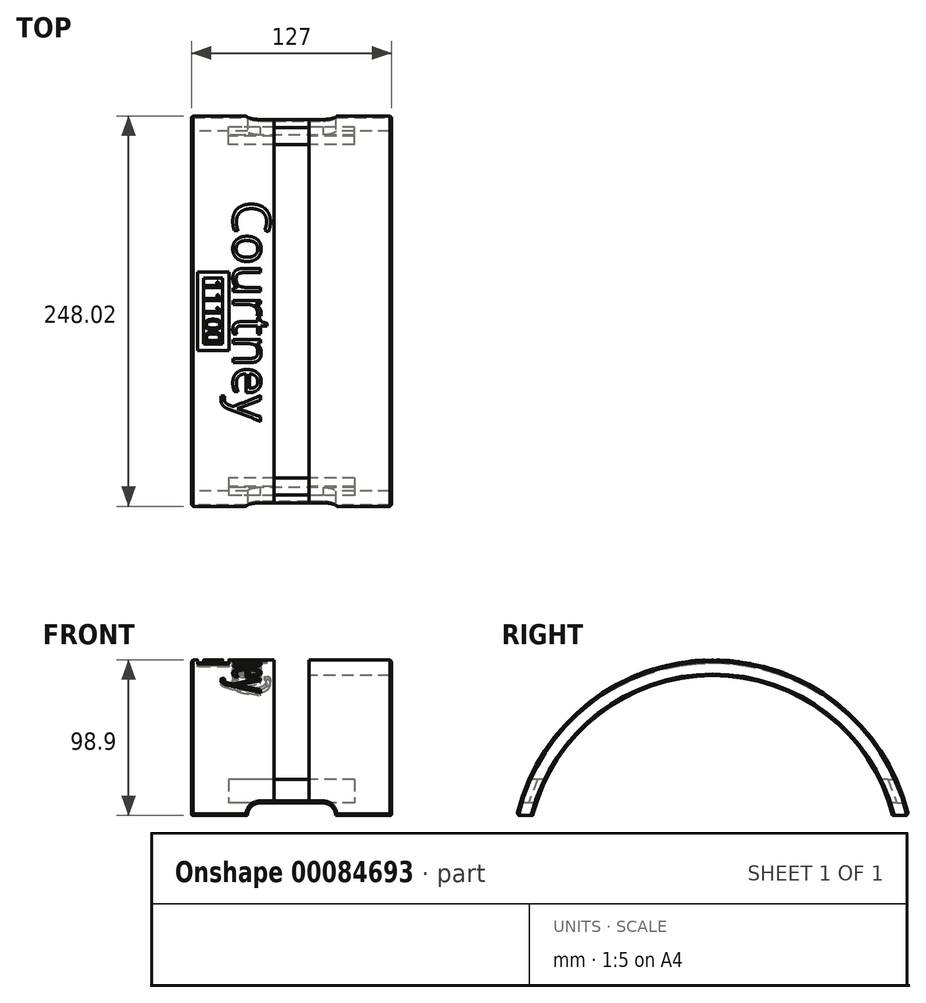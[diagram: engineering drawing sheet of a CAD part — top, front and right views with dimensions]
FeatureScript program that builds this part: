
annotation { "Feature Type Name" : "Feature", "Feature Type Description" : "" }
export const myFeature = defineFeature(function(context is Context, id is Id, definition is map)
    precondition{}
    {
        {
            var Q0;
            Q0=qCreatedBy(makeId("Right.planeOp"),FACE);
            var sketch = newSketch(context, id + "F0", { "sketchPlane" : qUnion([Q0])});
            skArc(sketch, "E0", {"start": v(114.3, 0) * mm, "mid": v(0, 88.9) * mm, "end": v(-114.3, 0) * mm});
            skPoint(sketch, "E1", {"position": v(0, 88.9) * mm});
            skArc(sketch, "E2", {"start": v(124.3, 0) * mm, "mid": v(0, 98.9) * mm, "end": v(-124.3, 0) * mm});
            skLineSegment(sketch, "E3", {"start": v(-124.3, 0) * mm, "end": v(-114.3, 0) * mm});
            skLineSegment(sketch, "E4", {"start": v(124.3, 0) * mm, "end": v(114.3, 0) * mm});
            skLineSegment(sketch, "E5", {"start": v(0, 98.9) * mm, "end": v(0, 88.9) * mm, "construction": true});
            skLineSegment(sketch, "E6", {"start": v(-114.3, 0) * mm, "end": v(114.3, 0) * mm, "construction": true});
            skLineSegment(sketch, "E7", {"start": v(10, 98.9) * mm, "end": v(-10, 98.9) * mm, "construction": true});
            skPoint(sketch, "E8", {"position": v(0, 98.9) * mm});
            skLineSegment(sketch, "E9", {"start": v(119.06, 17.12) * mm, "end": v(-119.06, 17.12) * mm});
            skPoint(sketch, "E10", {"position": v(0, 17.12) * mm});
            skPoint(sketch, "E11", {"position": v(-119.06, 17.12) * mm});
            skPoint(sketch, "E12", {"position": v(119.06, 17.12) * mm});
            skSolve(sketch);
        }
        {
            var Q0;
            Q0=makeQuery(id+"F0.imprint","IMPRINT",FACE,{"disambiguationData":[TD([[makeQuery(id+"F0.imprint","IMPRINT",EDGE,{"derivedFrom":sQuery(id+"F0.wireOp",EDGE,"E0")}),-1.0]])]});
            extrude(context, id + "F1", {"entities" : qUnion([Q0]), "depth" : 127 * mm});
        }
        {
            var Q0;
            Q0=sQuery(id+"F0.wireOp",EDGE,"E7");
            cPlane(context, id + "F2", {"entities" : qUnion([Q0]), "cplaneType" : CPlaneType.LINE_ANGLE, "offset" : 150 * mm, "angle" : 0 * degree, "width" : 150 * mm, "height" : 150 * mm});
        }
        {
            var Q0;
            Q0=makeQuery(id+"F1.opExtrude","SWEPT_EDGE",EDGE,{"disambiguationData":[OSD([sQuery(id+"F0.wireOp",EDGE,"E2"),sQuery(id+"F0.wireOp",EDGE,"E3")])]});
            cPlane(context, id + "F3", {"entities" : qUnion([Q0]), "cplaneType" : CPlaneType.LINE_ANGLE, "offset" : 150 * mm, "angle" : 0 * degree, "width" : 150 * mm, "height" : 150 * mm});
        }
        {
            var Q0;
            Q0=qCreatedBy(id+"F3.planeOp",FACE);
            var sketch = newSketch(context, id + "F4", { "sketchPlane" : qUnion([Q0])});
            skLineSegment(sketch, "E13", {"start": v(0, 98.9) * mm, "end": v(127, 98.9) * mm});
            skLineSegment(sketch, "E14.0", {"start": v(127, 98.9) * mm, "end": v(127, 0) * mm});
            skLineSegment(sketch, "E15.0", {"start": v(127, 0) * mm, "end": v(0, 0) * mm});
            skLineSegment(sketch, "E16.0", {"start": v(0, 98.9) * mm, "end": v(0, 0) * mm});
            skPoint(sketch, "E17", {"position": v(63.5, 0) * mm});
            skLineSegment(sketch, "E18", {"start": v(43.5, 8) * mm, "end": v(83.5, 8) * mm});
            skPoint(sketch, "E19", {"position": v(63.5, 8) * mm});
            skArc(sketch, "E20", {"start": v(43.5, 8) * mm, "mid": v(37.84, 5.66) * mm, "end": v(35.5, 0) * mm});
            skArc(sketch, "E21", {"start": v(91.5, 0) * mm, "mid": v(89.16, 5.66) * mm, "end": v(83.5, 8) * mm});
            skPoint(sketch, "E22.positionSnap0", {"position": v(63.5, 98.9) * mm});
            skLineSegment(sketch, "E23.bottom", {"start": v(52.5, 23) * mm, "end": v(74.5, 23) * mm});
            skLineSegment(sketch, "E23.top", {"start": v(52.5, 98.9) * mm, "end": v(74.5, 98.9) * mm});
            skLineSegment(sketch, "E23.left", {"start": v(52.5, 23) * mm, "end": v(52.5, 98.9) * mm});
            skLineSegment(sketch, "E23.right", {"start": v(74.5, 23) * mm, "end": v(74.5, 98.9) * mm});
            skSolve(sketch);
        }
        {
            var Q0;
            Q0=makeQuery(id+"F4.imprint","IMPRINT",FACE,{"disambiguationData":[TD([[makeQuery(id+"F4.imprint","IMPRINT",EDGE,{"derivedFrom":sQuery(id+"F4.wireOp",EDGE,"E23.bottom")}),1.0]])]});
            var Q1;
            Q1=makeQuery(id+"F4.imprint","IMPRINT",FACE,{"disambiguationData":[TD([[makeQuery(id+"F4.imprint","IMPRINT",EDGE,{"derivedFrom":sQuery(id+"F4.wireOp",EDGE,"E18")}),-1.0]])]});
            extrude(context, id + "F5", {"entities" : qUnion([Q0, Q1]), "operationType" : NewBodyOperationType.REMOVE, "endBound" : BoundingType.THROUGH_ALL, "oppositeDirection" : true, "depth" : 25 * mm});
        }
        {
            var Q0;
            Q0=makeQuery(id+"F5.boolean.opBoolean","COPY",FACE,{"derivedFrom":makeQuery(id+"F5.opExtrude","SWEPT_FACE",FACE,{"disambiguationData":[OSD([sQuery(id+"F4.wireOp",EDGE,"E23.left")])]})});
            var Q1;
            Q1=makeQuery(id+"F5.boolean.opBoolean","COPY",FACE,{"derivedFrom":makeQuery(id+"F5.opExtrude","SWEPT_FACE",FACE,{"disambiguationData":[OSD([sQuery(id+"F4.wireOp",EDGE,"E23.right")])]})});
            cPlane(context, id + "F6", {"entities" : qUnion([Q0, Q1]), "cplaneType" : CPlaneType.MID_PLANE, "offset" : 150 * mm, "width" : 150 * mm, "height" : 150 * mm});
        }
        {
            var Q0;
            Q0=qCreatedBy(id+"F6.planeOp",FACE);
            var sketch = newSketch(context, id + "F7", { "sketchPlane" : qUnion([Q0])});
            skArc(sketch, "E24.0", {"start": v(114.3, 0) * mm, "mid": v(0, 88.9) * mm, "end": v(-114.3, 0) * mm});
            skLineSegment(sketch, "E25.0", {"start": v(-111.96, 8) * mm, "end": v(-122.18, 8) * mm});
            skLineSegment(sketch, "E26.0", {"start": v(-105.83, 23) * mm, "end": v(-116.63, 23) * mm});
            skLineSegment(sketch, "E27", {"start": v(-111.23, 23) * mm, "end": v(-117.07, 8) * mm});
            skArc(sketch, "E28.0", {"start": v(124.3, 0) * mm, "mid": v(0, 98.9) * mm, "end": v(-124.3, 0) * mm});
            skLineSegment(sketch, "E29", {"start": v(0, 0) * mm, "end": v(0, 150) * mm, "construction": true});
            skPoint(sketch, "E29.endSnap0", {"position": v(0, 98.9) * mm});
            skLineSegment(sketch, "E30", {"start": v(75, 0) * mm, "end": v(-75, 0) * mm, "construction": true});
            skPoint(sketch, "E31", {"position": v(0, 0) * mm});
            skSolve(sketch);
        }
        {
            var Q0;
            {var subQ5=sQuery(id+"F7.wireOp",EDGE,"E27");Q0=makeQuery(id+"F7.imprint","IMPRINT",FACE,{"disambiguationData":[TD([[makeQuery(id+"F7.imprint","IMPRINT",EDGE,{"derivedFrom":subQ5}),1.0]])]});}
            extrude(context, id + "F8", {"entities" : qUnion([Q0]), "endBound" : BoundingType.SYMMETRIC, "depth" : 80 * mm});
        }
        {
            var Q0;
            {var subQ3=sQuery(id+"F7.wireOp",EDGE,"E27");Q0=makeQuery(id+"F7.imprint","IMPRINT",FACE,{"disambiguationData":[TD([[makeQuery(id+"F7.imprint","IMPRINT",EDGE,{"derivedFrom":subQ3}),-1.0]])]});}
            var Q1;
            Q1=makeQuery(id+"F5.boolean.opBoolean","COPY",FACE,{"derivedFrom":makeQuery(id+"F5.opExtrude","SWEPT_FACE",FACE,{"disambiguationData":[OSD([sQuery(id+"F4.wireOp",EDGE,"E23.right")])]})});
            extrude(context, id + "F9", {"entities" : qUnion([Q0]), "endBound" : BoundingType.UP_TO_SURFACE, "endBoundEntityFace" : qUnion([Q1]), "depth" : 25 * mm});
        }
        {
            var Q0;
            Q0=makeQuery(id+"F9.opExtrude","SWEPT_BODY",BODY,{"disambiguationData":[OSD([sQuery(id+"F7.wireOp",EDGE,"E25.0"),sQuery(id+"F7.wireOp",EDGE,"E26.0"),sQuery(id+"F7.wireOp",EDGE,"E27"),sQuery(id+"F7.wireOp",EDGE,"E28.0")])]});
            var Q1;
            {var subQ3=sQuery(id+"F7.wireOp",EDGE,"E27");Q1=makeQuery(id+"F7.imprint","IMPRINT",FACE,{"disambiguationData":[TD([[makeQuery(id+"F7.imprint","IMPRINT",EDGE,{"derivedFrom":subQ3}),-1.0]])]});}
            mirror(context, id + "F10", {"entities" : qUnion([Q0]), "mirrorPlane" : qUnion([Q1])});
        }
        {
            var Q0;
            Q0=makeQuery(id+"F10.opPattern","COPY",BODY,{"derivedFrom":makeQuery(id+"F9.opExtrude","SWEPT_BODY",BODY,{"disambiguationData":[OSD([sQuery(id+"F7.wireOp",EDGE,"E25.0"),sQuery(id+"F7.wireOp",EDGE,"E26.0"),sQuery(id+"F7.wireOp",EDGE,"E27"),sQuery(id+"F7.wireOp",EDGE,"E28.0")])]}),"instanceName":"1"});
            var Q1;
            Q1=makeQuery(id+"F9.opExtrude","SWEPT_BODY",BODY,{"disambiguationData":[OSD([sQuery(id+"F7.wireOp",EDGE,"E25.0"),sQuery(id+"F7.wireOp",EDGE,"E26.0"),sQuery(id+"F7.wireOp",EDGE,"E27"),sQuery(id+"F7.wireOp",EDGE,"E28.0")])]});
            var Q2;
            Q2=makeQuery(id+"F8.opExtrude","SWEPT_BODY",BODY,{"disambiguationData":[OSD([sQuery(id+"F7.wireOp",EDGE,"E24.0"),sQuery(id+"F7.wireOp",EDGE,"E25.0"),sQuery(id+"F7.wireOp",EDGE,"E26.0"),sQuery(id+"F7.wireOp",EDGE,"E27")])]});
            var Q3;
            Q3=makeQuery(id+"F1.opExtrude","SWEPT_BODY",BODY,{"disambiguationData":[OSD([sQuery(id+"F0.wireOp",EDGE,"E0"),sQuery(id+"F0.wireOp",EDGE,"E2"),sQuery(id+"F0.wireOp",EDGE,"E3"),sQuery(id+"F0.wireOp",EDGE,"E4")])]});
            booleanBodies(context, id + "F11", {"operationType" : BooleanOperationType.SUBTRACTION, "tools" : qUnion([Q0, Q1, Q2]), "targets" : qUnion([Q3]), "keepTools" : true});
        }
        {
            var Q0;
            Q0=makeQuery(id+"F10.opPattern","COPY",BODY,{"derivedFrom":makeQuery(id+"F9.opExtrude","SWEPT_BODY",BODY,{"disambiguationData":[OSD([sQuery(id+"F7.wireOp",EDGE,"E25.0"),sQuery(id+"F7.wireOp",EDGE,"E26.0"),sQuery(id+"F7.wireOp",EDGE,"E27"),sQuery(id+"F7.wireOp",EDGE,"E28.0")])]}),"instanceName":"1"});
            var Q1;
            Q1=makeQuery(id+"F9.opExtrude","SWEPT_BODY",BODY,{"disambiguationData":[OSD([sQuery(id+"F7.wireOp",EDGE,"E25.0"),sQuery(id+"F7.wireOp",EDGE,"E26.0"),sQuery(id+"F7.wireOp",EDGE,"E27"),sQuery(id+"F7.wireOp",EDGE,"E28.0")])]});
            var Q2;
            Q2=makeQuery(id+"F8.opExtrude","SWEPT_BODY",BODY,{"disambiguationData":[OSD([sQuery(id+"F7.wireOp",EDGE,"E24.0"),sQuery(id+"F7.wireOp",EDGE,"E25.0"),sQuery(id+"F7.wireOp",EDGE,"E26.0"),sQuery(id+"F7.wireOp",EDGE,"E27")])]});
            booleanBodies(context, id + "F12", {"operationType" : BooleanOperationType.UNION, "tools" : qUnion([Q0, Q1, Q2])});
        }
        {
            var Q0;
            Q0=makeQuery(id+"F10.opPattern","COPY",BODY,{"derivedFrom":makeQuery(id+"F9.opExtrude","SWEPT_BODY",BODY,{"disambiguationData":[OSD([sQuery(id+"F7.wireOp",EDGE,"E25.0"),sQuery(id+"F7.wireOp",EDGE,"E26.0"),sQuery(id+"F7.wireOp",EDGE,"E27"),sQuery(id+"F7.wireOp",EDGE,"E28.0")])]}),"instanceName":"1"});
            var Q1;
            Q1=qCreatedBy(makeId("Front.planeOp"),FACE);
            mirror(context, id + "F13", {"entities" : qUnion([Q0]), "mirrorPlane" : qUnion([Q1])});
        }
        {
            var Q0;
            Q0=makeQuery(id+"F13.opPattern","COPY",BODY,{"derivedFrom":makeQuery(id+"F10.opPattern","COPY",BODY,{"derivedFrom":makeQuery(id+"F9.opExtrude","SWEPT_BODY",BODY,{"disambiguationData":[OSD([sQuery(id+"F7.wireOp",EDGE,"E25.0"),sQuery(id+"F7.wireOp",EDGE,"E26.0"),sQuery(id+"F7.wireOp",EDGE,"E27"),sQuery(id+"F7.wireOp",EDGE,"E28.0")])]}),"instanceName":"1"}),"instanceName":"1"});
            var Q1;
            Q1=makeQuery(id+"F1.opExtrude","SWEPT_BODY",BODY,{"disambiguationData":[OSD([sQuery(id+"F0.wireOp",EDGE,"E0"),sQuery(id+"F0.wireOp",EDGE,"E2"),sQuery(id+"F0.wireOp",EDGE,"E3"),sQuery(id+"F0.wireOp",EDGE,"E4")])]});
            booleanBodies(context, id + "F14", {"operationType" : BooleanOperationType.SUBTRACTION, "tools" : qUnion([Q0]), "targets" : qUnion([Q1]), "keepTools" : true});
        }
        {
            var Q0;
            Q0=makeQuery(id+"F1.opExtrude","CAP_EDGE",EDGE,{"disambiguationData":[OSD([sQuery(id+"F0.wireOp",EDGE,"E2")])],"isStart":true});
            var Q1;
            Q1=makeQuery(id+"F1.opExtrude","CAP_EDGE",EDGE,{"disambiguationData":[OSD([sQuery(id+"F0.wireOp",EDGE,"E0")])],"isStart":true});
            var Q2;
            Q2=makeQuery(id+"F5.boolean.opBoolean","INTERSECT",EDGE,{"disambiguationData":[OD(1.0)],"derivedFrom":[makeQuery(id+"F1.opExtrude","SWEPT_FACE",FACE,{"disambiguationData":[OSD([sQuery(id+"F0.wireOp",EDGE,"E2")])]}),makeQuery(id+"F5.opExtrude","SWEPT_FACE",FACE,{"disambiguationData":[OSD([sQuery(id+"F4.wireOp",EDGE,"E21")])]})]});
            var Q3;
            {var subQ0=makeQuery(id+"F5.opExtrude","SWEPT_FACE",FACE,{"disambiguationData":[OSD([sQuery(id+"F4.wireOp",EDGE,"E18")])]});var subQ2=makeQuery(id+"F1.opExtrude","SWEPT_FACE",FACE,{"disambiguationData":[OSD([sQuery(id+"F0.wireOp",EDGE,"E2")])]});Q3=makeQuery(id+"F14.opBoolean","SPLIT",EDGE,{"disambiguationData":[TD([makeQuery(id+"F5.boolean.opBoolean","COPY",FACE,{"derivedFrom":makeQuery(id+"F5.opExtrude","SWEPT_FACE",FACE,{"disambiguationData":[OSD([sQuery(id+"F4.wireOp",EDGE,"E23.right")])]})})])],"derivedFrom":makeQuery(id+"F5.boolean.opBoolean","INTERSECT",EDGE,{"disambiguationData":[OD(1.0)],"derivedFrom":[subQ2,subQ0]})});}
            var Q4;
            {var subQ0=makeQuery(id+"F9.opExtrude","SWEPT_EDGE",EDGE,{"disambiguationData":[OSD([sQuery(id+"F7.wireOp",EDGE,"E25.0"),sQuery(id+"F7.wireOp",EDGE,"E28.0")])]});Q4=makeQuery(id+"F13.opPattern","COPY",EDGE,{"derivedFrom":makeQuery(id+"F12.opBoolean","MERGE",EDGE,{"derivedFrom":[subQ0,makeQuery(id+"F10.opPattern","COPY",EDGE,{"derivedFrom":subQ0,"instanceName":"1"})]}),"instanceName":"1"});}
            var Q5;
            Q5=makeQuery(id+"F5.boolean.opBoolean","INTERSECT",EDGE,{"disambiguationData":[OD(1.0)],"derivedFrom":[makeQuery(id+"F1.opExtrude","SWEPT_FACE",FACE,{"disambiguationData":[OSD([sQuery(id+"F0.wireOp",EDGE,"E2")])]}),makeQuery(id+"F5.opExtrude","SWEPT_FACE",FACE,{"disambiguationData":[OSD([sQuery(id+"F4.wireOp",EDGE,"E20")])]})]});
            var Q6;
            {var subQ0=makeQuery(id+"F5.opExtrude","SWEPT_FACE",FACE,{"disambiguationData":[OSD([sQuery(id+"F4.wireOp",EDGE,"E18")])]});var subQ1=makeQuery(id+"F1.opExtrude","SWEPT_FACE",FACE,{"disambiguationData":[OSD([sQuery(id+"F0.wireOp",EDGE,"E2")])]});Q6=makeQuery(id+"F14.opBoolean","SPLIT",EDGE,{"disambiguationData":[TD([makeQuery(id+"F5.boolean.opBoolean","COPY",FACE,{"derivedFrom":makeQuery(id+"F5.opExtrude","SWEPT_FACE",FACE,{"disambiguationData":[OSD([sQuery(id+"F4.wireOp",EDGE,"E23.left")])]})})])],"derivedFrom":makeQuery(id+"F5.boolean.opBoolean","INTERSECT",EDGE,{"disambiguationData":[OD(1.0)],"derivedFrom":[subQ1,subQ0]})});}
            var Q7;
            {var subQ0=sQuery(id+"F0.wireOp",EDGE,"E4");var subQ1=sQuery(id+"F0.wireOp",EDGE,"E2");Q7=makeQuery(id+"F5.boolean.opBoolean","SPLIT",EDGE,{"disambiguationData":[TD([makeQuery(id+"F5.opExtrude","SWEPT_FACE",FACE,{"disambiguationData":[OSD([sQuery(id+"F4.wireOp",EDGE,"E21")])]})])],"derivedFrom":makeQuery(id+"F1.opExtrude","SWEPT_EDGE",EDGE,{"disambiguationData":[OSD([subQ1,subQ0])]})});}
            var Q8;
            Q8=makeQuery(id+"F1.opExtrude","CAP_EDGE",EDGE,{"disambiguationData":[OSD([sQuery(id+"F0.wireOp",EDGE,"E2")])],"isStart":false});
            var Q9;
            Q9=makeQuery(id+"F1.opExtrude","CAP_EDGE",EDGE,{"disambiguationData":[OSD([sQuery(id+"F0.wireOp",EDGE,"E0")])],"isStart":false});
            var Q10;
            {var subQ0=sQuery(id+"F0.wireOp",EDGE,"E4");var subQ1=sQuery(id+"F0.wireOp",EDGE,"E2");Q10=makeQuery(id+"F5.boolean.opBoolean","SPLIT",EDGE,{"disambiguationData":[TD([makeQuery(id+"F5.opExtrude","SWEPT_FACE",FACE,{"disambiguationData":[OSD([sQuery(id+"F4.wireOp",EDGE,"E20")])]})])],"derivedFrom":makeQuery(id+"F1.opExtrude","SWEPT_EDGE",EDGE,{"disambiguationData":[OSD([subQ1,subQ0])]})});}
            var Q11;
            Q11=makeQuery(id+"F5.boolean.opBoolean","INTERSECT",EDGE,{"disambiguationData":[OD(0.0)],"derivedFrom":[makeQuery(id+"F1.opExtrude","SWEPT_FACE",FACE,{"disambiguationData":[OSD([sQuery(id+"F0.wireOp",EDGE,"E2")])]}),makeQuery(id+"F5.opExtrude","SWEPT_FACE",FACE,{"disambiguationData":[OSD([sQuery(id+"F4.wireOp",EDGE,"E20")])]})]});
            var Q12;
            {var subQ0=makeQuery(id+"F5.opExtrude","SWEPT_FACE",FACE,{"disambiguationData":[OSD([sQuery(id+"F4.wireOp",EDGE,"E18")])]});var subQ1=makeQuery(id+"F1.opExtrude","SWEPT_FACE",FACE,{"disambiguationData":[OSD([sQuery(id+"F0.wireOp",EDGE,"E2")])]});Q12=makeQuery(id+"F11.opBoolean","SPLIT",EDGE,{"disambiguationData":[TD([makeQuery(id+"F5.boolean.opBoolean","COPY",FACE,{"derivedFrom":makeQuery(id+"F5.opExtrude","SWEPT_FACE",FACE,{"disambiguationData":[OSD([sQuery(id+"F4.wireOp",EDGE,"E23.left")])]})})])],"derivedFrom":makeQuery(id+"F5.boolean.opBoolean","INTERSECT",EDGE,{"disambiguationData":[OD(0.0)],"derivedFrom":[subQ1,subQ0]})});}
            var Q13;
            {var subQ0=makeQuery(id+"F9.opExtrude","SWEPT_EDGE",EDGE,{"disambiguationData":[OSD([sQuery(id+"F7.wireOp",EDGE,"E25.0"),sQuery(id+"F7.wireOp",EDGE,"E28.0")])]});Q13=makeQuery(id+"F12.opBoolean","MERGE",EDGE,{"derivedFrom":[subQ0,makeQuery(id+"F10.opPattern","COPY",EDGE,{"derivedFrom":subQ0,"instanceName":"1"})]});}
            var Q14;
            {var subQ0=makeQuery(id+"F5.opExtrude","SWEPT_FACE",FACE,{"disambiguationData":[OSD([sQuery(id+"F4.wireOp",EDGE,"E18")])]});var subQ1=makeQuery(id+"F1.opExtrude","SWEPT_FACE",FACE,{"disambiguationData":[OSD([sQuery(id+"F0.wireOp",EDGE,"E2")])]});Q14=makeQuery(id+"F11.opBoolean","SPLIT",EDGE,{"disambiguationData":[TD([makeQuery(id+"F5.boolean.opBoolean","COPY",FACE,{"derivedFrom":makeQuery(id+"F5.opExtrude","SWEPT_FACE",FACE,{"disambiguationData":[OSD([sQuery(id+"F4.wireOp",EDGE,"E23.right")])]})})])],"derivedFrom":makeQuery(id+"F5.boolean.opBoolean","INTERSECT",EDGE,{"disambiguationData":[OD(0.0)],"derivedFrom":[subQ1,subQ0]})});}
            var Q15;
            Q15=makeQuery(id+"F5.boolean.opBoolean","INTERSECT",EDGE,{"disambiguationData":[OD(0.0)],"derivedFrom":[makeQuery(id+"F1.opExtrude","SWEPT_FACE",FACE,{"disambiguationData":[OSD([sQuery(id+"F0.wireOp",EDGE,"E2")])]}),makeQuery(id+"F5.opExtrude","SWEPT_FACE",FACE,{"disambiguationData":[OSD([sQuery(id+"F4.wireOp",EDGE,"E21")])]})]});
            var Q16;
            {var subQ0=sQuery(id+"F0.wireOp",EDGE,"E3");var subQ1=sQuery(id+"F0.wireOp",EDGE,"E2");Q16=makeQuery(id+"F5.boolean.opBoolean","SPLIT",EDGE,{"disambiguationData":[TD([makeQuery(id+"F5.opExtrude","SWEPT_FACE",FACE,{"disambiguationData":[OSD([sQuery(id+"F4.wireOp",EDGE,"E21")])]})])],"derivedFrom":makeQuery(id+"F1.opExtrude","SWEPT_EDGE",EDGE,{"disambiguationData":[OSD([subQ1,subQ0])]})});}
            var Q17;
            {var subQ0=sQuery(id+"F0.wireOp",EDGE,"E3");var subQ1=sQuery(id+"F0.wireOp",EDGE,"E2");Q17=makeQuery(id+"F5.boolean.opBoolean","SPLIT",EDGE,{"disambiguationData":[TD([makeQuery(id+"F5.opExtrude","SWEPT_FACE",FACE,{"disambiguationData":[OSD([sQuery(id+"F4.wireOp",EDGE,"E20")])]})])],"derivedFrom":makeQuery(id+"F1.opExtrude","SWEPT_EDGE",EDGE,{"disambiguationData":[OSD([subQ1,subQ0])]})});}
            chamfer(context, id + "F15", {"entities" : qUnion([Q0, Q1, Q2, Q3, Q4, Q5, Q6, Q7, Q8, Q9, Q10, Q11, Q12, Q13, Q14, Q15, Q16, Q17]), "width" : 1 * mm});
        }
        {
            var Q0;
            {var subQ0=sQuery(id+"F0.wireOp",EDGE,"E3");var subQ1=sQuery(id+"F0.wireOp",EDGE,"E2");var subQ2=makeQuery(id+"F5.opExtrude","SWEPT_FACE",FACE,{"disambiguationData":[OSD([sQuery(id+"F4.wireOp",EDGE,"E20")])]});var subQ3=makeQuery(id+"F1.opExtrude","SWEPT_FACE",FACE,{"disambiguationData":[OSD([subQ1])]});Q0=makeQuery(id+"F15.opChamfer","BLEND_EDGE",EDGE,{"blendedFrom":[makeQuery(id+"F5.boolean.opBoolean","INTERSECT",EDGE,{"disambiguationData":[OD(0.0)],"derivedFrom":[subQ3,subQ2]}),makeQuery(id+"F5.boolean.opBoolean","SPLIT",EDGE,{"disambiguationData":[TD([subQ2])],"derivedFrom":makeQuery(id+"F1.opExtrude","SWEPT_EDGE",EDGE,{"disambiguationData":[OSD([subQ1,subQ0])]})})],"blendedInto":[]});}
            var Q1;
            {var subQ0=sQuery(id+"F0.wireOp",EDGE,"E3");var subQ1=sQuery(id+"F0.wireOp",EDGE,"E2");Q1=makeQuery(id+"F15.opChamfer","BLEND_EDGE",EDGE,{"blendedFrom":[makeQuery(id+"F1.opExtrude","CAP_EDGE",EDGE,{"disambiguationData":[OSD([subQ1])],"isStart":true}),makeQuery(id+"F5.boolean.opBoolean","SPLIT",EDGE,{"disambiguationData":[TD([makeQuery(id+"F5.opExtrude","SWEPT_FACE",FACE,{"disambiguationData":[OSD([sQuery(id+"F4.wireOp",EDGE,"E20")])]})])],"derivedFrom":makeQuery(id+"F1.opExtrude","SWEPT_EDGE",EDGE,{"disambiguationData":[OSD([subQ1,subQ0])]})})],"blendedInto":[]});}
            var Q2;
            {var subQ0=sQuery(id+"F0.wireOp",EDGE,"E3");var subQ1=sQuery(id+"F0.wireOp",EDGE,"E2");var subQ2=makeQuery(id+"F1.opExtrude","SWEPT_FACE",FACE,{"disambiguationData":[OSD([subQ1])]});var subQ3=makeQuery(id+"F5.opExtrude","SWEPT_FACE",FACE,{"disambiguationData":[OSD([sQuery(id+"F4.wireOp",EDGE,"E21")])]});Q2=makeQuery(id+"F15.opChamfer","BLEND_EDGE",EDGE,{"blendedFrom":[makeQuery(id+"F5.boolean.opBoolean","INTERSECT",EDGE,{"disambiguationData":[OD(0.0)],"derivedFrom":[subQ2,subQ3]}),makeQuery(id+"F5.boolean.opBoolean","SPLIT",EDGE,{"disambiguationData":[TD([subQ3])],"derivedFrom":makeQuery(id+"F1.opExtrude","SWEPT_EDGE",EDGE,{"disambiguationData":[OSD([subQ1,subQ0])]})})],"blendedInto":[]});}
            var Q3;
            {var subQ0=sQuery(id+"F0.wireOp",EDGE,"E3");var subQ1=sQuery(id+"F0.wireOp",EDGE,"E2");Q3=makeQuery(id+"F15.opChamfer","BLEND_EDGE",EDGE,{"blendedFrom":[makeQuery(id+"F1.opExtrude","CAP_EDGE",EDGE,{"disambiguationData":[OSD([subQ1])],"isStart":false}),makeQuery(id+"F5.boolean.opBoolean","SPLIT",EDGE,{"disambiguationData":[TD([makeQuery(id+"F5.opExtrude","SWEPT_FACE",FACE,{"disambiguationData":[OSD([sQuery(id+"F4.wireOp",EDGE,"E21")])]})])],"derivedFrom":makeQuery(id+"F1.opExtrude","SWEPT_EDGE",EDGE,{"disambiguationData":[OSD([subQ1,subQ0])]})})],"blendedInto":[]});}
            var Q4;
            {var subQ0=sQuery(id+"F0.wireOp",EDGE,"E4");var subQ1=sQuery(id+"F0.wireOp",EDGE,"E2");Q4=makeQuery(id+"F15.opChamfer","BLEND_EDGE",EDGE,{"blendedFrom":[makeQuery(id+"F1.opExtrude","CAP_EDGE",EDGE,{"disambiguationData":[OSD([subQ1])],"isStart":false}),makeQuery(id+"F5.boolean.opBoolean","SPLIT",EDGE,{"disambiguationData":[TD([makeQuery(id+"F5.opExtrude","SWEPT_FACE",FACE,{"disambiguationData":[OSD([sQuery(id+"F4.wireOp",EDGE,"E21")])]})])],"derivedFrom":makeQuery(id+"F1.opExtrude","SWEPT_EDGE",EDGE,{"disambiguationData":[OSD([subQ1,subQ0])]})})],"blendedInto":[]});}
            var Q5;
            {var subQ0=makeQuery(id+"F5.opExtrude","SWEPT_FACE",FACE,{"disambiguationData":[OSD([sQuery(id+"F4.wireOp",EDGE,"E21")])]});var subQ1=sQuery(id+"F0.wireOp",EDGE,"E2");var subQ2=makeQuery(id+"F1.opExtrude","SWEPT_FACE",FACE,{"disambiguationData":[OSD([subQ1])]});var subQ3=sQuery(id+"F0.wireOp",EDGE,"E4");Q5=makeQuery(id+"F15.opChamfer","BLEND_EDGE",EDGE,{"blendedFrom":[makeQuery(id+"F5.boolean.opBoolean","SPLIT",EDGE,{"disambiguationData":[TD([subQ0])],"derivedFrom":makeQuery(id+"F1.opExtrude","SWEPT_EDGE",EDGE,{"disambiguationData":[OSD([subQ1,subQ3])]})}),makeQuery(id+"F5.boolean.opBoolean","INTERSECT",EDGE,{"disambiguationData":[OD(1.0)],"derivedFrom":[subQ2,subQ0]})],"blendedInto":[]});}
            var Q6;
            {var subQ0=makeQuery(id+"F5.opExtrude","SWEPT_FACE",FACE,{"disambiguationData":[OSD([sQuery(id+"F4.wireOp",EDGE,"E20")])]});var subQ1=sQuery(id+"F0.wireOp",EDGE,"E2");var subQ2=makeQuery(id+"F1.opExtrude","SWEPT_FACE",FACE,{"disambiguationData":[OSD([subQ1])]});var subQ3=sQuery(id+"F0.wireOp",EDGE,"E4");Q6=makeQuery(id+"F15.opChamfer","BLEND_EDGE",EDGE,{"blendedFrom":[makeQuery(id+"F5.boolean.opBoolean","SPLIT",EDGE,{"disambiguationData":[TD([subQ0])],"derivedFrom":makeQuery(id+"F1.opExtrude","SWEPT_EDGE",EDGE,{"disambiguationData":[OSD([subQ1,subQ3])]})}),makeQuery(id+"F5.boolean.opBoolean","INTERSECT",EDGE,{"disambiguationData":[OD(1.0)],"derivedFrom":[subQ2,subQ0]})],"blendedInto":[]});}
            var Q7;
            {var subQ0=sQuery(id+"F0.wireOp",EDGE,"E4");var subQ1=sQuery(id+"F0.wireOp",EDGE,"E2");Q7=makeQuery(id+"F15.opChamfer","BLEND_EDGE",EDGE,{"blendedFrom":[makeQuery(id+"F1.opExtrude","CAP_EDGE",EDGE,{"disambiguationData":[OSD([subQ1])],"isStart":true}),makeQuery(id+"F5.boolean.opBoolean","SPLIT",EDGE,{"disambiguationData":[TD([makeQuery(id+"F5.opExtrude","SWEPT_FACE",FACE,{"disambiguationData":[OSD([sQuery(id+"F4.wireOp",EDGE,"E20")])]})])],"derivedFrom":makeQuery(id+"F1.opExtrude","SWEPT_EDGE",EDGE,{"disambiguationData":[OSD([subQ1,subQ0])]})})],"blendedInto":[]});}
            var Q8;
            Q8=makeQuery(id+"F1.opExtrude","CAP_EDGE",EDGE,{"disambiguationData":[OSD([sQuery(id+"F0.wireOp",EDGE,"E4")])],"isStart":true});
            var Q9;
            Q9=makeQuery(id+"F1.opExtrude","CAP_EDGE",EDGE,{"disambiguationData":[OSD([sQuery(id+"F0.wireOp",EDGE,"E4")])],"isStart":false});
            var Q10;
            Q10=makeQuery(id+"F1.opExtrude","CAP_EDGE",EDGE,{"disambiguationData":[OSD([sQuery(id+"F0.wireOp",EDGE,"E3")])],"isStart":true});
            var Q11;
            Q11=makeQuery(id+"F1.opExtrude","CAP_EDGE",EDGE,{"disambiguationData":[OSD([sQuery(id+"F0.wireOp",EDGE,"E3")])],"isStart":false});
            fillet(context, id + "F16", {"entities" : qUnion([Q0, Q1, Q2, Q3, Q4, Q5, Q6, Q7, Q8, Q9, Q10, Q11]), "radius" : 1 * mm, "tangentPropagation" : true, "allowEdgeOverflow" : false});
        }
        {
            var Q0;
            Q0=qCreatedBy(makeId("Top.planeOp"),FACE);
            cPlane(context, id + "F17", {"entities" : qUnion([Q0]), "cplaneType" : CPlaneType.OFFSET, "offset" : 102 * mm, "width" : 150 * mm, "height" : 150 * mm});
        }
        {
            var Q0;
            Q0=qCreatedBy(id+"F17.planeOp",FACE);
            var sketch = newSketch(context, id + "F18", { "sketchPlane" : qUnion([Q0])});
            skText(sketch, "E32", { "text": "Courtney", "fontName": "OpenSans-Regular.ttf"});
            skLineSegment(sketch, "E33.0", {"start": v(52.5, 121.78) * mm, "end": v(52.5, -121.78) * mm});
            skLineSegment(sketch, "E34.0", {"start": v(33.87, 124) * mm, "end": v(1.8, 124) * mm});
            skLineSegment(sketch, "E35.0", {"start": v(1, 123.84) * mm, "end": v(1, -123.84) * mm});
            skLineSegment(sketch, "E36.0", {"start": v(1.8, -124) * mm, "end": v(33.87, -124) * mm});
            skLineSegment(sketch, "E37.top", {"start": v(52.5, -121.78) * mm, "end": v(1, -121.78) * mm});
            skText(sketch, "E38", { "text": "11100", "fontName": "OpenSans-Regular.ttf"});
            skLineSegment(sketch, "E39", {"start": v(26.5, 0) * mm, "end": v(18.87, 0) * mm, "construction": true});
            skLineSegment(sketch, "E40", {"start": v(8.62, 0) * mm, "end": v(1, 0) * mm, "construction": true});
            skLineSegment(sketch, "E41.bottom", {"start": v(19.75, -21) * mm, "end": v(7.75, -21) * mm});
            skLineSegment(sketch, "E41.top", {"start": v(19.75, 21) * mm, "end": v(7.75, 21) * mm});
            skLineSegment(sketch, "E41.left", {"start": v(19.75, -21) * mm, "end": v(19.75, 21) * mm});
            skLineSegment(sketch, "E41.right", {"start": v(7.75, -21) * mm, "end": v(7.75, 21) * mm});
            skPoint(sketch, "E41.middle", {"position": v(13.75, 0) * mm});
            skLineSegment(sketch, "E42.bottom", {"start": v(23.75, -25) * mm, "end": v(3.75, -25) * mm});
            skLineSegment(sketch, "E42.top", {"start": v(23.75, 25) * mm, "end": v(3.75, 25) * mm});
            skLineSegment(sketch, "E42.left", {"start": v(23.75, -25) * mm, "end": v(23.75, 25) * mm});
            skLineSegment(sketch, "E42.right", {"start": v(3.75, -25) * mm, "end": v(3.75, 25) * mm});
            skLineSegment(sketch, "E43", {"start": v(13.75, -25) * mm, "end": v(13.75, -21) * mm, "construction": true});
            skLineSegment(sketch, "E44", {"start": v(23.75, 0) * mm, "end": v(19.75, 0) * mm, "construction": true});
            skLineSegment(sketch, "E45", {"start": v(23.75, -0.91) * mm, "end": v(19.75, -0.91) * mm, "construction": true});
            const initialGuessF18  = {"E32": [0.0265, 0.07, 0, -1, 0.0235], "E38": [0.00862, 0.02, 0, -1, 0.01025]};
            skSetInitialGuess(sketch, initialGuessF18);
            skSolve(sketch);
        }
        {
            var Q0;
            Q0=makeQuery(id+"F18.imprint","IMPRINT",FACE,{"disambiguationData":[TD([[makeQuery(id+"F18.imprint","IMPRINT",EDGE,{"derivedFrom":sQuery(id+"F18.wireOp",EDGE,"E38.sketch_text.stroke-27")}),-1.0]])]});
            var Q1;
            Q1=makeQuery(id+"F18.imprint","IMPRINT",FACE,{"disambiguationData":[TD([[makeQuery(id+"F18.imprint","IMPRINT",EDGE,{"derivedFrom":sQuery(id+"F18.wireOp",EDGE,"E38.sketch_text.stroke-43")}),-1.0]])]});
            var Q2;
            Q2=makeQuery(id+"F18.imprint","IMPRINT",FACE,{"disambiguationData":[TD([[makeQuery(id+"F18.imprint","IMPRINT",EDGE,{"derivedFrom":sQuery(id+"F18.wireOp",EDGE,"E38.sketch_text.stroke-18")}),-1.0]])]});
            var Q3;
            Q3=makeQuery(id+"F18.imprint","IMPRINT",FACE,{"disambiguationData":[TD([[makeQuery(id+"F18.imprint","IMPRINT",EDGE,{"derivedFrom":sQuery(id+"F18.wireOp",EDGE,"E38.sketch_text.stroke-9")}),-1.0]])]});
            var Q4;
            Q4=makeQuery(id+"F18.imprint","IMPRINT",FACE,{"disambiguationData":[TD([[makeQuery(id+"F18.imprint","IMPRINT",EDGE,{"derivedFrom":sQuery(id+"F18.wireOp",EDGE,"E38.sketch_text.stroke-0")}),-1.0]])]});
            var Q5;
            Q5=makeQuery(id+"F18.imprint","IMPRINT",FACE,{"disambiguationData":[TD([[makeQuery(id+"F18.imprint","IMPRINT",EDGE,{"derivedFrom":sQuery(id+"F18.wireOp",EDGE,"E41.bottom")}),1.0]])]});
            var Q6;
            Q6=makeQuery(id+"F18.imprint","IMPRINT",FACE,{"disambiguationData":[TD([[makeQuery(id+"F18.imprint","IMPRINT",EDGE,{"derivedFrom":sQuery(id+"F18.wireOp",EDGE,"E32.sketch_text.stroke-15")}),-1.0]])]});
            var Q7;
            Q7=makeQuery(id+"F18.imprint","IMPRINT",FACE,{"disambiguationData":[TD([[makeQuery(id+"F18.imprint","IMPRINT",EDGE,{"derivedFrom":sQuery(id+"F18.wireOp",EDGE,"E32.sketch_text.stroke-0")}),-1.0]])]});
            var Q8;
            Q8=makeQuery(id+"F18.imprint","IMPRINT",FACE,{"disambiguationData":[TD([[makeQuery(id+"F18.imprint","IMPRINT",EDGE,{"derivedFrom":sQuery(id+"F18.wireOp",EDGE,"E32.sketch_text.stroke-32")}),-1.0]])]});
            var Q9;
            Q9=makeQuery(id+"F18.imprint","IMPRINT",FACE,{"disambiguationData":[TD([[makeQuery(id+"F18.imprint","IMPRINT",EDGE,{"derivedFrom":sQuery(id+"F18.wireOp",EDGE,"E32.sketch_text.stroke-49")}),-1.0]])]});
            var Q10;
            Q10=makeQuery(id+"F18.imprint","IMPRINT",FACE,{"disambiguationData":[TD([[makeQuery(id+"F18.imprint","IMPRINT",EDGE,{"derivedFrom":sQuery(id+"F18.wireOp",EDGE,"E32.sketch_text.stroke-62")}),-1.0]])]});
            var Q11;
            Q11=makeQuery(id+"F18.imprint","IMPRINT",FACE,{"disambiguationData":[TD([[makeQuery(id+"F18.imprint","IMPRINT",EDGE,{"derivedFrom":sQuery(id+"F18.wireOp",EDGE,"E32.sketch_text.stroke-81")}),-1.0]])]});
            var Q12;
            Q12=makeQuery(id+"F18.imprint","IMPRINT",FACE,{"disambiguationData":[TD([[makeQuery(id+"F18.imprint","IMPRINT",EDGE,{"derivedFrom":sQuery(id+"F18.wireOp",EDGE,"E32.sketch_text.stroke-98")}),-1.0]])]});
            var Q13;
            Q13=makeQuery(id+"F18.imprint","IMPRINT",FACE,{"disambiguationData":[TD([[makeQuery(id+"F18.imprint","IMPRINT",EDGE,{"derivedFrom":sQuery(id+"F18.wireOp",EDGE,"E32.sketch_text.stroke-117")}),-1.0]])]});
            var Q14;
            {var subQ4=sQuery(id+"F0.wireOp",EDGE,"E2");Q14=makeQuery(id+"F14.opBoolean","SPLIT",FACE,{"disambiguationData":[TD([makeQuery(id+"F5.boolean.opBoolean","COPY",FACE,{"derivedFrom":makeQuery(id+"F5.opExtrude","SWEPT_FACE",FACE,{"disambiguationData":[OSD([sQuery(id+"F4.wireOp",EDGE,"E23.left")])]})})])],"derivedFrom":makeQuery(id+"F1.opExtrude","SWEPT_FACE",FACE,{"disambiguationData":[OSD([subQ4])]})});}
            extrude(context, id + "F19", {"entities" : qUnion([Q0, Q1, Q2, Q3, Q4, Q5, Q6, Q7, Q8, Q9, Q10, Q11, Q12, Q13]), "endBound" : BoundingType.UP_TO_SURFACE, "oppositeDirection" : true, "endBoundEntityFace" : qUnion([Q14]), "depth" : 25 * mm});
        }
        {
            var Q0;
            Q0=makeQuery(id+"F19.opExtrude","SWEPT_BODY",BODY,{"disambiguationData":[OSD([sQuery(id+"F18.wireOp",EDGE,"E32.sketch_text.stroke-0"),sQuery(id+"F18.wireOp",EDGE,"E32.sketch_text.stroke-1"),sQuery(id+"F18.wireOp",EDGE,"E32.sketch_text.stroke-2"),sQuery(id+"F18.wireOp",EDGE,"E32.sketch_text.stroke-3"),sQuery(id+"F18.wireOp",EDGE,"E32.sketch_text.stroke-4"),sQuery(id+"F18.wireOp",EDGE,"E32.sketch_text.stroke-5"),sQuery(id+"F18.wireOp",EDGE,"E32.sketch_text.stroke-6"),sQuery(id+"F18.wireOp",EDGE,"E32.sketch_text.stroke-7"),sQuery(id+"F18.wireOp",EDGE,"E32.sketch_text.stroke-8"),sQuery(id+"F18.wireOp",EDGE,"E32.sketch_text.stroke-9"),sQuery(id+"F18.wireOp",EDGE,"E32.sketch_text.stroke-10"),sQuery(id+"F18.wireOp",EDGE,"E32.sketch_text.stroke-11"),sQuery(id+"F18.wireOp",EDGE,"E32.sketch_text.stroke-12"),sQuery(id+"F18.wireOp",EDGE,"E32.sketch_text.stroke-13"),sQuery(id+"F18.wireOp",EDGE,"E32.sketch_text.stroke-14")])]});
            var Q1;
            Q1=makeQuery(id+"F19.opExtrude","SWEPT_BODY",BODY,{"disambiguationData":[OSD([sQuery(id+"F18.wireOp",EDGE,"E32.sketch_text.stroke-15"),sQuery(id+"F18.wireOp",EDGE,"E32.sketch_text.stroke-16"),sQuery(id+"F18.wireOp",EDGE,"E32.sketch_text.stroke-17"),sQuery(id+"F18.wireOp",EDGE,"E32.sketch_text.stroke-18"),sQuery(id+"F18.wireOp",EDGE,"E32.sketch_text.stroke-19"),sQuery(id+"F18.wireOp",EDGE,"E32.sketch_text.stroke-20"),sQuery(id+"F18.wireOp",EDGE,"E32.sketch_text.stroke-21"),sQuery(id+"F18.wireOp",EDGE,"E32.sketch_text.stroke-22"),sQuery(id+"F18.wireOp",EDGE,"E32.sketch_text.stroke-23"),sQuery(id+"F18.wireOp",EDGE,"E32.sketch_text.stroke-24"),sQuery(id+"F18.wireOp",EDGE,"E32.sketch_text.stroke-25"),sQuery(id+"F18.wireOp",EDGE,"E32.sketch_text.stroke-26"),sQuery(id+"F18.wireOp",EDGE,"E32.sketch_text.stroke-27"),sQuery(id+"F18.wireOp",EDGE,"E32.sketch_text.stroke-28"),sQuery(id+"F18.wireOp",EDGE,"E32.sketch_text.stroke-29"),sQuery(id+"F18.wireOp",EDGE,"E32.sketch_text.stroke-30"),sQuery(id+"F18.wireOp",EDGE,"E32.sketch_text.stroke-31")])]});
            var Q2;
            Q2=makeQuery(id+"F19.opExtrude","SWEPT_BODY",BODY,{"disambiguationData":[OSD([sQuery(id+"F18.wireOp",EDGE,"E32.sketch_text.stroke-32"),sQuery(id+"F18.wireOp",EDGE,"E32.sketch_text.stroke-33"),sQuery(id+"F18.wireOp",EDGE,"E32.sketch_text.stroke-34"),sQuery(id+"F18.wireOp",EDGE,"E32.sketch_text.stroke-35"),sQuery(id+"F18.wireOp",EDGE,"E32.sketch_text.stroke-36"),sQuery(id+"F18.wireOp",EDGE,"E32.sketch_text.stroke-37"),sQuery(id+"F18.wireOp",EDGE,"E32.sketch_text.stroke-38"),sQuery(id+"F18.wireOp",EDGE,"E32.sketch_text.stroke-39"),sQuery(id+"F18.wireOp",EDGE,"E32.sketch_text.stroke-40"),sQuery(id+"F18.wireOp",EDGE,"E32.sketch_text.stroke-41"),sQuery(id+"F18.wireOp",EDGE,"E32.sketch_text.stroke-42"),sQuery(id+"F18.wireOp",EDGE,"E32.sketch_text.stroke-43"),sQuery(id+"F18.wireOp",EDGE,"E32.sketch_text.stroke-44"),sQuery(id+"F18.wireOp",EDGE,"E32.sketch_text.stroke-45"),sQuery(id+"F18.wireOp",EDGE,"E32.sketch_text.stroke-46"),sQuery(id+"F18.wireOp",EDGE,"E32.sketch_text.stroke-47"),sQuery(id+"F18.wireOp",EDGE,"E32.sketch_text.stroke-48")])]});
            var Q3;
            Q3=makeQuery(id+"F19.opExtrude","SWEPT_BODY",BODY,{"disambiguationData":[OSD([sQuery(id+"F18.wireOp",EDGE,"E32.sketch_text.stroke-49"),sQuery(id+"F18.wireOp",EDGE,"E32.sketch_text.stroke-50"),sQuery(id+"F18.wireOp",EDGE,"E32.sketch_text.stroke-51"),sQuery(id+"F18.wireOp",EDGE,"E32.sketch_text.stroke-52"),sQuery(id+"F18.wireOp",EDGE,"E32.sketch_text.stroke-53"),sQuery(id+"F18.wireOp",EDGE,"E32.sketch_text.stroke-54"),sQuery(id+"F18.wireOp",EDGE,"E32.sketch_text.stroke-55"),sQuery(id+"F18.wireOp",EDGE,"E32.sketch_text.stroke-56"),sQuery(id+"F18.wireOp",EDGE,"E32.sketch_text.stroke-57"),sQuery(id+"F18.wireOp",EDGE,"E32.sketch_text.stroke-58"),sQuery(id+"F18.wireOp",EDGE,"E32.sketch_text.stroke-59"),sQuery(id+"F18.wireOp",EDGE,"E32.sketch_text.stroke-60"),sQuery(id+"F18.wireOp",EDGE,"E32.sketch_text.stroke-61")])]});
            var Q4;
            Q4=makeQuery(id+"F19.opExtrude","SWEPT_BODY",BODY,{"disambiguationData":[OSD([sQuery(id+"F18.wireOp",EDGE,"E32.sketch_text.stroke-62"),sQuery(id+"F18.wireOp",EDGE,"E32.sketch_text.stroke-63"),sQuery(id+"F18.wireOp",EDGE,"E32.sketch_text.stroke-64"),sQuery(id+"F18.wireOp",EDGE,"E32.sketch_text.stroke-65"),sQuery(id+"F18.wireOp",EDGE,"E32.sketch_text.stroke-66"),sQuery(id+"F18.wireOp",EDGE,"E32.sketch_text.stroke-67"),sQuery(id+"F18.wireOp",EDGE,"E32.sketch_text.stroke-68"),sQuery(id+"F18.wireOp",EDGE,"E32.sketch_text.stroke-69"),sQuery(id+"F18.wireOp",EDGE,"E32.sketch_text.stroke-70"),sQuery(id+"F18.wireOp",EDGE,"E32.sketch_text.stroke-71"),sQuery(id+"F18.wireOp",EDGE,"E32.sketch_text.stroke-72"),sQuery(id+"F18.wireOp",EDGE,"E32.sketch_text.stroke-73"),sQuery(id+"F18.wireOp",EDGE,"E32.sketch_text.stroke-74"),sQuery(id+"F18.wireOp",EDGE,"E32.sketch_text.stroke-75"),sQuery(id+"F18.wireOp",EDGE,"E32.sketch_text.stroke-76"),sQuery(id+"F18.wireOp",EDGE,"E32.sketch_text.stroke-77"),sQuery(id+"F18.wireOp",EDGE,"E32.sketch_text.stroke-78"),sQuery(id+"F18.wireOp",EDGE,"E32.sketch_text.stroke-79"),sQuery(id+"F18.wireOp",EDGE,"E32.sketch_text.stroke-80")])]});
            var Q5;
            Q5=makeQuery(id+"F19.opExtrude","SWEPT_BODY",BODY,{"disambiguationData":[OSD([sQuery(id+"F18.wireOp",EDGE,"E32.sketch_text.stroke-81"),sQuery(id+"F18.wireOp",EDGE,"E32.sketch_text.stroke-82"),sQuery(id+"F18.wireOp",EDGE,"E32.sketch_text.stroke-83"),sQuery(id+"F18.wireOp",EDGE,"E32.sketch_text.stroke-84"),sQuery(id+"F18.wireOp",EDGE,"E32.sketch_text.stroke-85"),sQuery(id+"F18.wireOp",EDGE,"E32.sketch_text.stroke-86"),sQuery(id+"F18.wireOp",EDGE,"E32.sketch_text.stroke-87"),sQuery(id+"F18.wireOp",EDGE,"E32.sketch_text.stroke-88"),sQuery(id+"F18.wireOp",EDGE,"E32.sketch_text.stroke-89"),sQuery(id+"F18.wireOp",EDGE,"E32.sketch_text.stroke-90"),sQuery(id+"F18.wireOp",EDGE,"E32.sketch_text.stroke-91"),sQuery(id+"F18.wireOp",EDGE,"E32.sketch_text.stroke-92"),sQuery(id+"F18.wireOp",EDGE,"E32.sketch_text.stroke-93"),sQuery(id+"F18.wireOp",EDGE,"E32.sketch_text.stroke-94"),sQuery(id+"F18.wireOp",EDGE,"E32.sketch_text.stroke-95"),sQuery(id+"F18.wireOp",EDGE,"E32.sketch_text.stroke-96"),sQuery(id+"F18.wireOp",EDGE,"E32.sketch_text.stroke-97")])]});
            var Q6;
            Q6=makeQuery(id+"F19.opExtrude","SWEPT_BODY",BODY,{"disambiguationData":[OSD([sQuery(id+"F18.wireOp",EDGE,"E32.sketch_text.stroke-98"),sQuery(id+"F18.wireOp",EDGE,"E32.sketch_text.stroke-99"),sQuery(id+"F18.wireOp",EDGE,"E32.sketch_text.stroke-100"),sQuery(id+"F18.wireOp",EDGE,"E32.sketch_text.stroke-101"),sQuery(id+"F18.wireOp",EDGE,"E32.sketch_text.stroke-102"),sQuery(id+"F18.wireOp",EDGE,"E32.sketch_text.stroke-103"),sQuery(id+"F18.wireOp",EDGE,"E32.sketch_text.stroke-104"),sQuery(id+"F18.wireOp",EDGE,"E32.sketch_text.stroke-105"),sQuery(id+"F18.wireOp",EDGE,"E32.sketch_text.stroke-106"),sQuery(id+"F18.wireOp",EDGE,"E32.sketch_text.stroke-107"),sQuery(id+"F18.wireOp",EDGE,"E32.sketch_text.stroke-108"),sQuery(id+"F18.wireOp",EDGE,"E32.sketch_text.stroke-109"),sQuery(id+"F18.wireOp",EDGE,"E32.sketch_text.stroke-110"),sQuery(id+"F18.wireOp",EDGE,"E32.sketch_text.stroke-111"),sQuery(id+"F18.wireOp",EDGE,"E32.sketch_text.stroke-112"),sQuery(id+"F18.wireOp",EDGE,"E32.sketch_text.stroke-113"),sQuery(id+"F18.wireOp",EDGE,"E32.sketch_text.stroke-114"),sQuery(id+"F18.wireOp",EDGE,"E32.sketch_text.stroke-115"),sQuery(id+"F18.wireOp",EDGE,"E32.sketch_text.stroke-116")])]});
            var Q7;
            Q7=makeQuery(id+"F19.opExtrude","SWEPT_BODY",BODY,{"disambiguationData":[OSD([sQuery(id+"F18.wireOp",EDGE,"E32.sketch_text.stroke-117"),sQuery(id+"F18.wireOp",EDGE,"E32.sketch_text.stroke-118"),sQuery(id+"F18.wireOp",EDGE,"E32.sketch_text.stroke-119"),sQuery(id+"F18.wireOp",EDGE,"E32.sketch_text.stroke-120"),sQuery(id+"F18.wireOp",EDGE,"E32.sketch_text.stroke-121"),sQuery(id+"F18.wireOp",EDGE,"E32.sketch_text.stroke-122"),sQuery(id+"F18.wireOp",EDGE,"E32.sketch_text.stroke-123"),sQuery(id+"F18.wireOp",EDGE,"E32.sketch_text.stroke-124"),sQuery(id+"F18.wireOp",EDGE,"E32.sketch_text.stroke-125"),sQuery(id+"F18.wireOp",EDGE,"E32.sketch_text.stroke-126"),sQuery(id+"F18.wireOp",EDGE,"E32.sketch_text.stroke-127"),sQuery(id+"F18.wireOp",EDGE,"E32.sketch_text.stroke-128"),sQuery(id+"F18.wireOp",EDGE,"E32.sketch_text.stroke-129"),sQuery(id+"F18.wireOp",EDGE,"E32.sketch_text.stroke-130"),sQuery(id+"F18.wireOp",EDGE,"E32.sketch_text.stroke-131"),sQuery(id+"F18.wireOp",EDGE,"E32.sketch_text.stroke-132")])]});
            var Q8;
            Q8=makeQuery(id+"F19.opExtrude","SWEPT_BODY",BODY,{"disambiguationData":[OSD([sQuery(id+"F18.wireOp",EDGE,"E41.bottom"),sQuery(id+"F18.wireOp",EDGE,"E41.top"),sQuery(id+"F18.wireOp",EDGE,"E41.left"),sQuery(id+"F18.wireOp",EDGE,"E41.right"),sQuery(id+"F18.wireOp",EDGE,"E42.bottom"),sQuery(id+"F18.wireOp",EDGE,"E42.top"),sQuery(id+"F18.wireOp",EDGE,"E42.left"),sQuery(id+"F18.wireOp",EDGE,"E42.right")])]});
            var Q9;
            Q9=makeQuery(id+"F19.opExtrude","SWEPT_BODY",BODY,{"disambiguationData":[OSD([sQuery(id+"F18.wireOp",EDGE,"E38.sketch_text.stroke-43"),sQuery(id+"F18.wireOp",EDGE,"E38.sketch_text.stroke-44"),sQuery(id+"F18.wireOp",EDGE,"E38.sketch_text.stroke-45"),sQuery(id+"F18.wireOp",EDGE,"E38.sketch_text.stroke-46"),sQuery(id+"F18.wireOp",EDGE,"E38.sketch_text.stroke-47"),sQuery(id+"F18.wireOp",EDGE,"E38.sketch_text.stroke-48"),sQuery(id+"F18.wireOp",EDGE,"E38.sketch_text.stroke-49"),sQuery(id+"F18.wireOp",EDGE,"E38.sketch_text.stroke-50"),sQuery(id+"F18.wireOp",EDGE,"E38.sketch_text.stroke-51"),sQuery(id+"F18.wireOp",EDGE,"E38.sketch_text.stroke-52"),sQuery(id+"F18.wireOp",EDGE,"E38.sketch_text.stroke-53"),sQuery(id+"F18.wireOp",EDGE,"E38.sketch_text.stroke-54"),sQuery(id+"F18.wireOp",EDGE,"E38.sketch_text.stroke-55"),sQuery(id+"F18.wireOp",EDGE,"E38.sketch_text.stroke-56"),sQuery(id+"F18.wireOp",EDGE,"E38.sketch_text.stroke-57"),sQuery(id+"F18.wireOp",EDGE,"E38.sketch_text.stroke-58")])]});
            var Q10;
            Q10=makeQuery(id+"F19.opExtrude","SWEPT_BODY",BODY,{"disambiguationData":[OSD([sQuery(id+"F18.wireOp",EDGE,"E38.sketch_text.stroke-27"),sQuery(id+"F18.wireOp",EDGE,"E38.sketch_text.stroke-28"),sQuery(id+"F18.wireOp",EDGE,"E38.sketch_text.stroke-29"),sQuery(id+"F18.wireOp",EDGE,"E38.sketch_text.stroke-30"),sQuery(id+"F18.wireOp",EDGE,"E38.sketch_text.stroke-31"),sQuery(id+"F18.wireOp",EDGE,"E38.sketch_text.stroke-32"),sQuery(id+"F18.wireOp",EDGE,"E38.sketch_text.stroke-33"),sQuery(id+"F18.wireOp",EDGE,"E38.sketch_text.stroke-34"),sQuery(id+"F18.wireOp",EDGE,"E38.sketch_text.stroke-35"),sQuery(id+"F18.wireOp",EDGE,"E38.sketch_text.stroke-36"),sQuery(id+"F18.wireOp",EDGE,"E38.sketch_text.stroke-37"),sQuery(id+"F18.wireOp",EDGE,"E38.sketch_text.stroke-38"),sQuery(id+"F18.wireOp",EDGE,"E38.sketch_text.stroke-39"),sQuery(id+"F18.wireOp",EDGE,"E38.sketch_text.stroke-40"),sQuery(id+"F18.wireOp",EDGE,"E38.sketch_text.stroke-41"),sQuery(id+"F18.wireOp",EDGE,"E38.sketch_text.stroke-42")])]});
            var Q11;
            Q11=makeQuery(id+"F19.opExtrude","SWEPT_BODY",BODY,{"disambiguationData":[OSD([sQuery(id+"F18.wireOp",EDGE,"E38.sketch_text.stroke-0"),sQuery(id+"F18.wireOp",EDGE,"E38.sketch_text.stroke-1"),sQuery(id+"F18.wireOp",EDGE,"E38.sketch_text.stroke-2"),sQuery(id+"F18.wireOp",EDGE,"E38.sketch_text.stroke-3"),sQuery(id+"F18.wireOp",EDGE,"E38.sketch_text.stroke-4"),sQuery(id+"F18.wireOp",EDGE,"E38.sketch_text.stroke-5"),sQuery(id+"F18.wireOp",EDGE,"E38.sketch_text.stroke-6"),sQuery(id+"F18.wireOp",EDGE,"E38.sketch_text.stroke-7"),sQuery(id+"F18.wireOp",EDGE,"E38.sketch_text.stroke-8")])]});
            var Q12;
            Q12=makeQuery(id+"F19.opExtrude","SWEPT_BODY",BODY,{"disambiguationData":[OSD([sQuery(id+"F18.wireOp",EDGE,"E38.sketch_text.stroke-9"),sQuery(id+"F18.wireOp",EDGE,"E38.sketch_text.stroke-10"),sQuery(id+"F18.wireOp",EDGE,"E38.sketch_text.stroke-11"),sQuery(id+"F18.wireOp",EDGE,"E38.sketch_text.stroke-12"),sQuery(id+"F18.wireOp",EDGE,"E38.sketch_text.stroke-13"),sQuery(id+"F18.wireOp",EDGE,"E38.sketch_text.stroke-14"),sQuery(id+"F18.wireOp",EDGE,"E38.sketch_text.stroke-15"),sQuery(id+"F18.wireOp",EDGE,"E38.sketch_text.stroke-16"),sQuery(id+"F18.wireOp",EDGE,"E38.sketch_text.stroke-17")])]});
            var Q13;
            Q13=makeQuery(id+"F19.opExtrude","SWEPT_BODY",BODY,{"disambiguationData":[OSD([sQuery(id+"F18.wireOp",EDGE,"E38.sketch_text.stroke-18"),sQuery(id+"F18.wireOp",EDGE,"E38.sketch_text.stroke-19"),sQuery(id+"F18.wireOp",EDGE,"E38.sketch_text.stroke-20"),sQuery(id+"F18.wireOp",EDGE,"E38.sketch_text.stroke-21"),sQuery(id+"F18.wireOp",EDGE,"E38.sketch_text.stroke-22"),sQuery(id+"F18.wireOp",EDGE,"E38.sketch_text.stroke-23"),sQuery(id+"F18.wireOp",EDGE,"E38.sketch_text.stroke-24"),sQuery(id+"F18.wireOp",EDGE,"E38.sketch_text.stroke-25"),sQuery(id+"F18.wireOp",EDGE,"E38.sketch_text.stroke-26")])]});
            transform(context, id + "F20", {"entities" : qUnion([Q0, Q1, Q2, Q3, Q4, Q5, Q6, Q7, Q8, Q9, Q10, Q11, Q12, Q13]), "transformType" : TransformType.TRANSLATION_3D, "dx" : 0 * mm, "dy" : 0 * mm, "dz" : -2 * mm, "makeCopy" : false});
        }
        {
            var Q0;
            Q0=makeQuery(id+"F19.opExtrude","SWEPT_BODY",BODY,{"disambiguationData":[OSD([sQuery(id+"F18.wireOp",EDGE,"E32.sketch_text.stroke-0"),sQuery(id+"F18.wireOp",EDGE,"E32.sketch_text.stroke-1"),sQuery(id+"F18.wireOp",EDGE,"E32.sketch_text.stroke-2"),sQuery(id+"F18.wireOp",EDGE,"E32.sketch_text.stroke-3"),sQuery(id+"F18.wireOp",EDGE,"E32.sketch_text.stroke-4"),sQuery(id+"F18.wireOp",EDGE,"E32.sketch_text.stroke-5"),sQuery(id+"F18.wireOp",EDGE,"E32.sketch_text.stroke-6"),sQuery(id+"F18.wireOp",EDGE,"E32.sketch_text.stroke-7"),sQuery(id+"F18.wireOp",EDGE,"E32.sketch_text.stroke-8"),sQuery(id+"F18.wireOp",EDGE,"E32.sketch_text.stroke-9"),sQuery(id+"F18.wireOp",EDGE,"E32.sketch_text.stroke-10"),sQuery(id+"F18.wireOp",EDGE,"E32.sketch_text.stroke-11"),sQuery(id+"F18.wireOp",EDGE,"E32.sketch_text.stroke-12"),sQuery(id+"F18.wireOp",EDGE,"E32.sketch_text.stroke-13"),sQuery(id+"F18.wireOp",EDGE,"E32.sketch_text.stroke-14")])]});
            var Q1;
            Q1=makeQuery(id+"F19.opExtrude","SWEPT_BODY",BODY,{"disambiguationData":[OSD([sQuery(id+"F18.wireOp",EDGE,"E32.sketch_text.stroke-15"),sQuery(id+"F18.wireOp",EDGE,"E32.sketch_text.stroke-16"),sQuery(id+"F18.wireOp",EDGE,"E32.sketch_text.stroke-17"),sQuery(id+"F18.wireOp",EDGE,"E32.sketch_text.stroke-18"),sQuery(id+"F18.wireOp",EDGE,"E32.sketch_text.stroke-19"),sQuery(id+"F18.wireOp",EDGE,"E32.sketch_text.stroke-20"),sQuery(id+"F18.wireOp",EDGE,"E32.sketch_text.stroke-21"),sQuery(id+"F18.wireOp",EDGE,"E32.sketch_text.stroke-22"),sQuery(id+"F18.wireOp",EDGE,"E32.sketch_text.stroke-23"),sQuery(id+"F18.wireOp",EDGE,"E32.sketch_text.stroke-24"),sQuery(id+"F18.wireOp",EDGE,"E32.sketch_text.stroke-25"),sQuery(id+"F18.wireOp",EDGE,"E32.sketch_text.stroke-26"),sQuery(id+"F18.wireOp",EDGE,"E32.sketch_text.stroke-27"),sQuery(id+"F18.wireOp",EDGE,"E32.sketch_text.stroke-28"),sQuery(id+"F18.wireOp",EDGE,"E32.sketch_text.stroke-29"),sQuery(id+"F18.wireOp",EDGE,"E32.sketch_text.stroke-30"),sQuery(id+"F18.wireOp",EDGE,"E32.sketch_text.stroke-31")])]});
            var Q2;
            Q2=makeQuery(id+"F19.opExtrude","SWEPT_BODY",BODY,{"disambiguationData":[OSD([sQuery(id+"F18.wireOp",EDGE,"E32.sketch_text.stroke-32"),sQuery(id+"F18.wireOp",EDGE,"E32.sketch_text.stroke-33"),sQuery(id+"F18.wireOp",EDGE,"E32.sketch_text.stroke-34"),sQuery(id+"F18.wireOp",EDGE,"E32.sketch_text.stroke-35"),sQuery(id+"F18.wireOp",EDGE,"E32.sketch_text.stroke-36"),sQuery(id+"F18.wireOp",EDGE,"E32.sketch_text.stroke-37"),sQuery(id+"F18.wireOp",EDGE,"E32.sketch_text.stroke-38"),sQuery(id+"F18.wireOp",EDGE,"E32.sketch_text.stroke-39"),sQuery(id+"F18.wireOp",EDGE,"E32.sketch_text.stroke-40"),sQuery(id+"F18.wireOp",EDGE,"E32.sketch_text.stroke-41"),sQuery(id+"F18.wireOp",EDGE,"E32.sketch_text.stroke-42"),sQuery(id+"F18.wireOp",EDGE,"E32.sketch_text.stroke-43"),sQuery(id+"F18.wireOp",EDGE,"E32.sketch_text.stroke-44"),sQuery(id+"F18.wireOp",EDGE,"E32.sketch_text.stroke-45"),sQuery(id+"F18.wireOp",EDGE,"E32.sketch_text.stroke-46"),sQuery(id+"F18.wireOp",EDGE,"E32.sketch_text.stroke-47"),sQuery(id+"F18.wireOp",EDGE,"E32.sketch_text.stroke-48")])]});
            var Q3;
            Q3=makeQuery(id+"F19.opExtrude","SWEPT_BODY",BODY,{"disambiguationData":[OSD([sQuery(id+"F18.wireOp",EDGE,"E41.bottom"),sQuery(id+"F18.wireOp",EDGE,"E41.top"),sQuery(id+"F18.wireOp",EDGE,"E41.left"),sQuery(id+"F18.wireOp",EDGE,"E41.right"),sQuery(id+"F18.wireOp",EDGE,"E42.bottom"),sQuery(id+"F18.wireOp",EDGE,"E42.top"),sQuery(id+"F18.wireOp",EDGE,"E42.left"),sQuery(id+"F18.wireOp",EDGE,"E42.right")])]});
            var Q4;
            Q4=makeQuery(id+"F19.opExtrude","SWEPT_BODY",BODY,{"disambiguationData":[OSD([sQuery(id+"F18.wireOp",EDGE,"E38.sketch_text.stroke-0"),sQuery(id+"F18.wireOp",EDGE,"E38.sketch_text.stroke-1"),sQuery(id+"F18.wireOp",EDGE,"E38.sketch_text.stroke-2"),sQuery(id+"F18.wireOp",EDGE,"E38.sketch_text.stroke-3"),sQuery(id+"F18.wireOp",EDGE,"E38.sketch_text.stroke-4"),sQuery(id+"F18.wireOp",EDGE,"E38.sketch_text.stroke-5"),sQuery(id+"F18.wireOp",EDGE,"E38.sketch_text.stroke-6"),sQuery(id+"F18.wireOp",EDGE,"E38.sketch_text.stroke-7"),sQuery(id+"F18.wireOp",EDGE,"E38.sketch_text.stroke-8")])]});
            var Q5;
            Q5=makeQuery(id+"F19.opExtrude","SWEPT_BODY",BODY,{"disambiguationData":[OSD([sQuery(id+"F18.wireOp",EDGE,"E38.sketch_text.stroke-9"),sQuery(id+"F18.wireOp",EDGE,"E38.sketch_text.stroke-10"),sQuery(id+"F18.wireOp",EDGE,"E38.sketch_text.stroke-11"),sQuery(id+"F18.wireOp",EDGE,"E38.sketch_text.stroke-12"),sQuery(id+"F18.wireOp",EDGE,"E38.sketch_text.stroke-13"),sQuery(id+"F18.wireOp",EDGE,"E38.sketch_text.stroke-14"),sQuery(id+"F18.wireOp",EDGE,"E38.sketch_text.stroke-15"),sQuery(id+"F18.wireOp",EDGE,"E38.sketch_text.stroke-16"),sQuery(id+"F18.wireOp",EDGE,"E38.sketch_text.stroke-17")])]});
            var Q6;
            Q6=makeQuery(id+"F19.opExtrude","SWEPT_BODY",BODY,{"disambiguationData":[OSD([sQuery(id+"F18.wireOp",EDGE,"E38.sketch_text.stroke-18"),sQuery(id+"F18.wireOp",EDGE,"E38.sketch_text.stroke-19"),sQuery(id+"F18.wireOp",EDGE,"E38.sketch_text.stroke-20"),sQuery(id+"F18.wireOp",EDGE,"E38.sketch_text.stroke-21"),sQuery(id+"F18.wireOp",EDGE,"E38.sketch_text.stroke-22"),sQuery(id+"F18.wireOp",EDGE,"E38.sketch_text.stroke-23"),sQuery(id+"F18.wireOp",EDGE,"E38.sketch_text.stroke-24"),sQuery(id+"F18.wireOp",EDGE,"E38.sketch_text.stroke-25"),sQuery(id+"F18.wireOp",EDGE,"E38.sketch_text.stroke-26")])]});
            var Q7;
            Q7=makeQuery(id+"F19.opExtrude","SWEPT_BODY",BODY,{"disambiguationData":[OSD([sQuery(id+"F18.wireOp",EDGE,"E38.sketch_text.stroke-27"),sQuery(id+"F18.wireOp",EDGE,"E38.sketch_text.stroke-28"),sQuery(id+"F18.wireOp",EDGE,"E38.sketch_text.stroke-29"),sQuery(id+"F18.wireOp",EDGE,"E38.sketch_text.stroke-30"),sQuery(id+"F18.wireOp",EDGE,"E38.sketch_text.stroke-31"),sQuery(id+"F18.wireOp",EDGE,"E38.sketch_text.stroke-32"),sQuery(id+"F18.wireOp",EDGE,"E38.sketch_text.stroke-33"),sQuery(id+"F18.wireOp",EDGE,"E38.sketch_text.stroke-34"),sQuery(id+"F18.wireOp",EDGE,"E38.sketch_text.stroke-35"),sQuery(id+"F18.wireOp",EDGE,"E38.sketch_text.stroke-36"),sQuery(id+"F18.wireOp",EDGE,"E38.sketch_text.stroke-37"),sQuery(id+"F18.wireOp",EDGE,"E38.sketch_text.stroke-38"),sQuery(id+"F18.wireOp",EDGE,"E38.sketch_text.stroke-39"),sQuery(id+"F18.wireOp",EDGE,"E38.sketch_text.stroke-40"),sQuery(id+"F18.wireOp",EDGE,"E38.sketch_text.stroke-41"),sQuery(id+"F18.wireOp",EDGE,"E38.sketch_text.stroke-42")])]});
            var Q8;
            Q8=makeQuery(id+"F19.opExtrude","SWEPT_BODY",BODY,{"disambiguationData":[OSD([sQuery(id+"F18.wireOp",EDGE,"E38.sketch_text.stroke-43"),sQuery(id+"F18.wireOp",EDGE,"E38.sketch_text.stroke-44"),sQuery(id+"F18.wireOp",EDGE,"E38.sketch_text.stroke-45"),sQuery(id+"F18.wireOp",EDGE,"E38.sketch_text.stroke-46"),sQuery(id+"F18.wireOp",EDGE,"E38.sketch_text.stroke-47"),sQuery(id+"F18.wireOp",EDGE,"E38.sketch_text.stroke-48"),sQuery(id+"F18.wireOp",EDGE,"E38.sketch_text.stroke-49"),sQuery(id+"F18.wireOp",EDGE,"E38.sketch_text.stroke-50"),sQuery(id+"F18.wireOp",EDGE,"E38.sketch_text.stroke-51"),sQuery(id+"F18.wireOp",EDGE,"E38.sketch_text.stroke-52"),sQuery(id+"F18.wireOp",EDGE,"E38.sketch_text.stroke-53"),sQuery(id+"F18.wireOp",EDGE,"E38.sketch_text.stroke-54"),sQuery(id+"F18.wireOp",EDGE,"E38.sketch_text.stroke-55"),sQuery(id+"F18.wireOp",EDGE,"E38.sketch_text.stroke-56"),sQuery(id+"F18.wireOp",EDGE,"E38.sketch_text.stroke-57"),sQuery(id+"F18.wireOp",EDGE,"E38.sketch_text.stroke-58")])]});
            var Q9;
            Q9=makeQuery(id+"F19.opExtrude","SWEPT_BODY",BODY,{"disambiguationData":[OSD([sQuery(id+"F18.wireOp",EDGE,"E32.sketch_text.stroke-49"),sQuery(id+"F18.wireOp",EDGE,"E32.sketch_text.stroke-50"),sQuery(id+"F18.wireOp",EDGE,"E32.sketch_text.stroke-51"),sQuery(id+"F18.wireOp",EDGE,"E32.sketch_text.stroke-52"),sQuery(id+"F18.wireOp",EDGE,"E32.sketch_text.stroke-53"),sQuery(id+"F18.wireOp",EDGE,"E32.sketch_text.stroke-54"),sQuery(id+"F18.wireOp",EDGE,"E32.sketch_text.stroke-55"),sQuery(id+"F18.wireOp",EDGE,"E32.sketch_text.stroke-56"),sQuery(id+"F18.wireOp",EDGE,"E32.sketch_text.stroke-57"),sQuery(id+"F18.wireOp",EDGE,"E32.sketch_text.stroke-58"),sQuery(id+"F18.wireOp",EDGE,"E32.sketch_text.stroke-59"),sQuery(id+"F18.wireOp",EDGE,"E32.sketch_text.stroke-60"),sQuery(id+"F18.wireOp",EDGE,"E32.sketch_text.stroke-61")])]});
            var Q10;
            Q10=makeQuery(id+"F19.opExtrude","SWEPT_BODY",BODY,{"disambiguationData":[OSD([sQuery(id+"F18.wireOp",EDGE,"E32.sketch_text.stroke-62"),sQuery(id+"F18.wireOp",EDGE,"E32.sketch_text.stroke-63"),sQuery(id+"F18.wireOp",EDGE,"E32.sketch_text.stroke-64"),sQuery(id+"F18.wireOp",EDGE,"E32.sketch_text.stroke-65"),sQuery(id+"F18.wireOp",EDGE,"E32.sketch_text.stroke-66"),sQuery(id+"F18.wireOp",EDGE,"E32.sketch_text.stroke-67"),sQuery(id+"F18.wireOp",EDGE,"E32.sketch_text.stroke-68"),sQuery(id+"F18.wireOp",EDGE,"E32.sketch_text.stroke-69"),sQuery(id+"F18.wireOp",EDGE,"E32.sketch_text.stroke-70"),sQuery(id+"F18.wireOp",EDGE,"E32.sketch_text.stroke-71"),sQuery(id+"F18.wireOp",EDGE,"E32.sketch_text.stroke-72"),sQuery(id+"F18.wireOp",EDGE,"E32.sketch_text.stroke-73"),sQuery(id+"F18.wireOp",EDGE,"E32.sketch_text.stroke-74"),sQuery(id+"F18.wireOp",EDGE,"E32.sketch_text.stroke-75"),sQuery(id+"F18.wireOp",EDGE,"E32.sketch_text.stroke-76"),sQuery(id+"F18.wireOp",EDGE,"E32.sketch_text.stroke-77"),sQuery(id+"F18.wireOp",EDGE,"E32.sketch_text.stroke-78"),sQuery(id+"F18.wireOp",EDGE,"E32.sketch_text.stroke-79"),sQuery(id+"F18.wireOp",EDGE,"E32.sketch_text.stroke-80")])]});
            var Q11;
            Q11=makeQuery(id+"F19.opExtrude","SWEPT_BODY",BODY,{"disambiguationData":[OSD([sQuery(id+"F18.wireOp",EDGE,"E32.sketch_text.stroke-98"),sQuery(id+"F18.wireOp",EDGE,"E32.sketch_text.stroke-99"),sQuery(id+"F18.wireOp",EDGE,"E32.sketch_text.stroke-100"),sQuery(id+"F18.wireOp",EDGE,"E32.sketch_text.stroke-101"),sQuery(id+"F18.wireOp",EDGE,"E32.sketch_text.stroke-102"),sQuery(id+"F18.wireOp",EDGE,"E32.sketch_text.stroke-103"),sQuery(id+"F18.wireOp",EDGE,"E32.sketch_text.stroke-104"),sQuery(id+"F18.wireOp",EDGE,"E32.sketch_text.stroke-105"),sQuery(id+"F18.wireOp",EDGE,"E32.sketch_text.stroke-106"),sQuery(id+"F18.wireOp",EDGE,"E32.sketch_text.stroke-107"),sQuery(id+"F18.wireOp",EDGE,"E32.sketch_text.stroke-108"),sQuery(id+"F18.wireOp",EDGE,"E32.sketch_text.stroke-109"),sQuery(id+"F18.wireOp",EDGE,"E32.sketch_text.stroke-110"),sQuery(id+"F18.wireOp",EDGE,"E32.sketch_text.stroke-111"),sQuery(id+"F18.wireOp",EDGE,"E32.sketch_text.stroke-112"),sQuery(id+"F18.wireOp",EDGE,"E32.sketch_text.stroke-113"),sQuery(id+"F18.wireOp",EDGE,"E32.sketch_text.stroke-114"),sQuery(id+"F18.wireOp",EDGE,"E32.sketch_text.stroke-115"),sQuery(id+"F18.wireOp",EDGE,"E32.sketch_text.stroke-116")])]});
            var Q12;
            Q12=makeQuery(id+"F19.opExtrude","SWEPT_BODY",BODY,{"disambiguationData":[OSD([sQuery(id+"F18.wireOp",EDGE,"E32.sketch_text.stroke-117"),sQuery(id+"F18.wireOp",EDGE,"E32.sketch_text.stroke-118"),sQuery(id+"F18.wireOp",EDGE,"E32.sketch_text.stroke-119"),sQuery(id+"F18.wireOp",EDGE,"E32.sketch_text.stroke-120"),sQuery(id+"F18.wireOp",EDGE,"E32.sketch_text.stroke-121"),sQuery(id+"F18.wireOp",EDGE,"E32.sketch_text.stroke-122"),sQuery(id+"F18.wireOp",EDGE,"E32.sketch_text.stroke-123"),sQuery(id+"F18.wireOp",EDGE,"E32.sketch_text.stroke-124"),sQuery(id+"F18.wireOp",EDGE,"E32.sketch_text.stroke-125"),sQuery(id+"F18.wireOp",EDGE,"E32.sketch_text.stroke-126"),sQuery(id+"F18.wireOp",EDGE,"E32.sketch_text.stroke-127"),sQuery(id+"F18.wireOp",EDGE,"E32.sketch_text.stroke-128"),sQuery(id+"F18.wireOp",EDGE,"E32.sketch_text.stroke-129"),sQuery(id+"F18.wireOp",EDGE,"E32.sketch_text.stroke-130"),sQuery(id+"F18.wireOp",EDGE,"E32.sketch_text.stroke-131"),sQuery(id+"F18.wireOp",EDGE,"E32.sketch_text.stroke-132")])]});
            var Q13;
            Q13=makeQuery(id+"F19.opExtrude","SWEPT_BODY",BODY,{"disambiguationData":[OSD([sQuery(id+"F18.wireOp",EDGE,"E32.sketch_text.stroke-81"),sQuery(id+"F18.wireOp",EDGE,"E32.sketch_text.stroke-82"),sQuery(id+"F18.wireOp",EDGE,"E32.sketch_text.stroke-83"),sQuery(id+"F18.wireOp",EDGE,"E32.sketch_text.stroke-84"),sQuery(id+"F18.wireOp",EDGE,"E32.sketch_text.stroke-85"),sQuery(id+"F18.wireOp",EDGE,"E32.sketch_text.stroke-86"),sQuery(id+"F18.wireOp",EDGE,"E32.sketch_text.stroke-87"),sQuery(id+"F18.wireOp",EDGE,"E32.sketch_text.stroke-88"),sQuery(id+"F18.wireOp",EDGE,"E32.sketch_text.stroke-89"),sQuery(id+"F18.wireOp",EDGE,"E32.sketch_text.stroke-90"),sQuery(id+"F18.wireOp",EDGE,"E32.sketch_text.stroke-91"),sQuery(id+"F18.wireOp",EDGE,"E32.sketch_text.stroke-92"),sQuery(id+"F18.wireOp",EDGE,"E32.sketch_text.stroke-93"),sQuery(id+"F18.wireOp",EDGE,"E32.sketch_text.stroke-94"),sQuery(id+"F18.wireOp",EDGE,"E32.sketch_text.stroke-95"),sQuery(id+"F18.wireOp",EDGE,"E32.sketch_text.stroke-96"),sQuery(id+"F18.wireOp",EDGE,"E32.sketch_text.stroke-97")])]});
            var Q14;
            Q14=makeQuery(id+"F14.opBoolean","SPLIT",BODY,{"disambiguationData":[OD(0.0)],"derivedFrom":makeQuery(id+"F1.opExtrude","SWEPT_BODY",BODY,{"disambiguationData":[OSD([sQuery(id+"F0.wireOp",EDGE,"E0"),sQuery(id+"F0.wireOp",EDGE,"E2"),sQuery(id+"F0.wireOp",EDGE,"E3"),sQuery(id+"F0.wireOp",EDGE,"E4")])]})});
            booleanBodies(context, id + "F21", {"operationType" : BooleanOperationType.SUBTRACTION, "tools" : qUnion([Q0, Q1, Q2, Q3, Q4, Q5, Q6, Q7, Q8, Q9, Q10, Q11, Q12, Q13]), "targets" : qUnion([Q14])});
        }
    });
